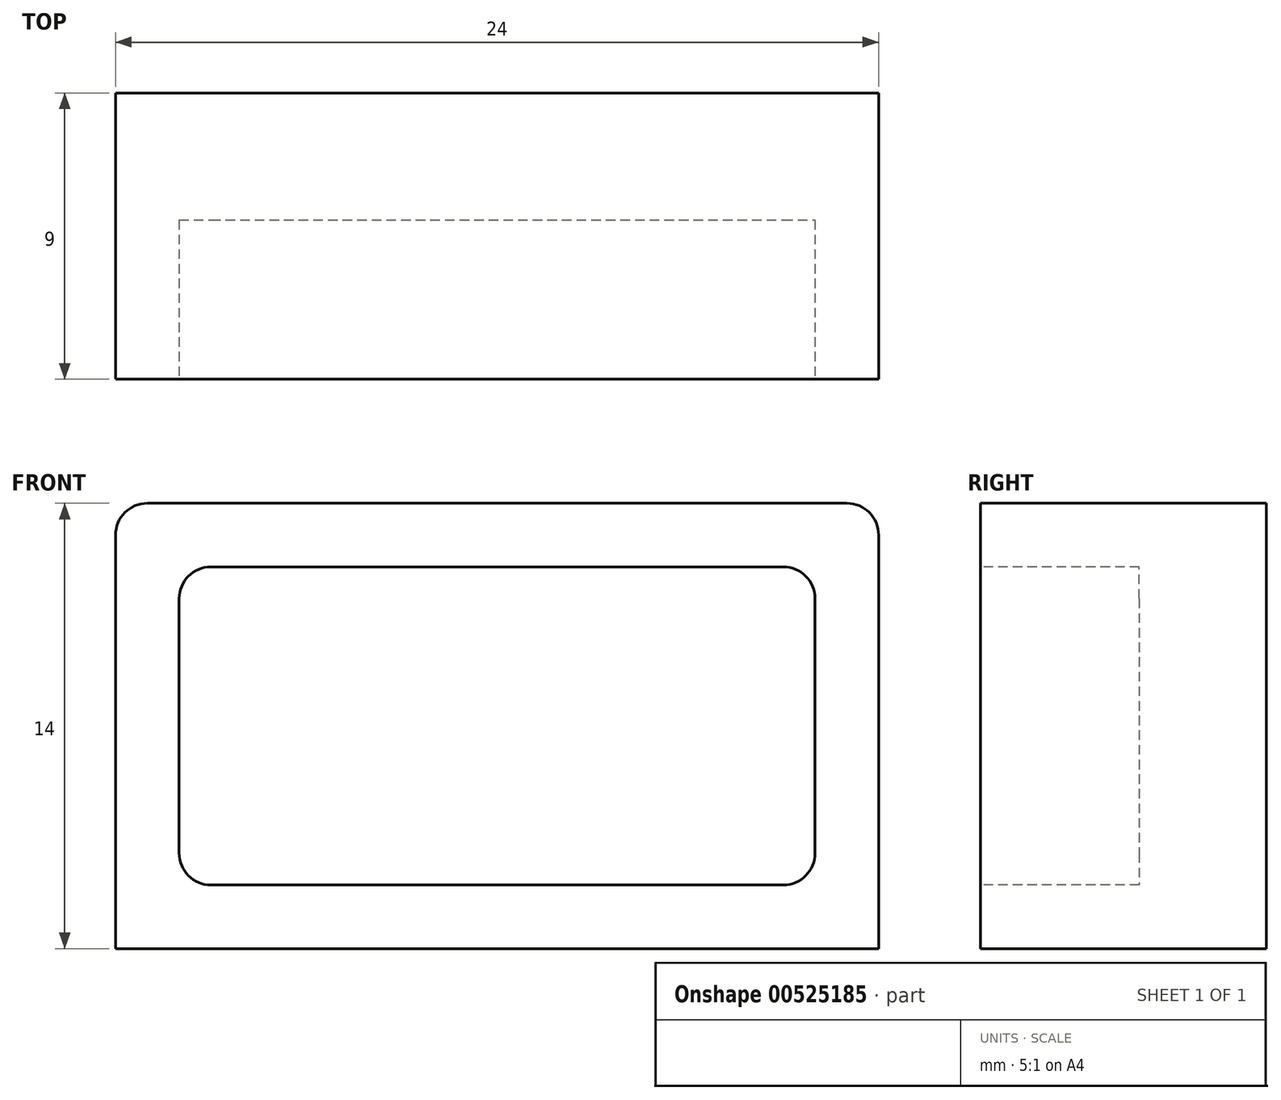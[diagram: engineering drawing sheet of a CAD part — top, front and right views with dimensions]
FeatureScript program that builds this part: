
annotation { "Feature Type Name" : "Feature", "Feature Type Description" : "" }
export const myFeature = defineFeature(function(context is Context, id is Id, definition is map)
    precondition{}
    {
        {
            assignVariable(context, id + "F0", {"name" : "DIFF", "anyValue" : 0 * mm});
        }
        {
            assignVariable(context, id + "F1", {"name" : "MAGNET_D", "anyValue" : 5 * mm + getVariable(context, 'DIFF')});
        }
        {
            assignVariable(context, id + "F2", {"name" : "PAD", "anyValue" : 2 * mm});
        }
        {
            assignVariable(context, id + "F3", {"name" : "D", "anyValue" : getVariable(context, 'MAGNET_D') + getVariable(context, 'PAD') * 2});
        }
        {
            var Q0;
            Q0=qCreatedBy(makeId("Front.planeOp"),FACE);
            var sketch = newSketch(context, id + "F4", { "sketchPlane" : qUnion([Q0])});
            skLineSegment(sketch, "E0.bottom", {"start": v(-12, 0) * mm, "end": v(12, 0) * mm});
            skLineSegment(sketch, "E0.top", {"start": v(-12, 14) * mm, "end": v(12, 14) * mm});
            skLineSegment(sketch, "E0.left", {"start": v(-12, 0) * mm, "end": v(-12, 14) * mm});
            skLineSegment(sketch, "E0.right", {"start": v(12, 0) * mm, "end": v(12, 14) * mm});
            skPoint(sketch, "E1", {"position": v(0, 0) * mm});
            skSolve(sketch);
        }
        {
            var Q0;
            Q0=makeQuery(id+"F4.imprint","IMPRINT",FACE,{"disambiguationData":[TD([[makeQuery(id+"F4.imprint","IMPRINT",EDGE,{"derivedFrom":sQuery(id+"F4.wireOp",EDGE,"E0.bottom")}),1.0]])]});
            extrude(context, id + "F5", {"entities" : qUnion([Q0]), "depth" : getVariable(context, 'D'), "offsetDistance" : 25 * mm});
        }
        {
            var Q0;
            Q0=makeQuery(id+"F5.opExtrude","CAP_FACE",FACE,{"disambiguationData":[OSD([sQuery(id+"F4.wireOp",EDGE,"E0.bottom"),sQuery(id+"F4.wireOp",EDGE,"E0.top"),sQuery(id+"F4.wireOp",EDGE,"E0.left"),sQuery(id+"F4.wireOp",EDGE,"E0.right")])],"isStart":false});
            var sketch = newSketch(context, id + "F6", { "sketchPlane" : qUnion([Q0])});
            skLineSegment(sketch, "E2.bottom", {"start": v(-10, 12) * mm, "end": v(10, 12) * mm});
            skLineSegment(sketch, "E2.top", {"start": v(-10, 2) * mm, "end": v(10, 2) * mm});
            skLineSegment(sketch, "E2.left", {"start": v(-10, 12) * mm, "end": v(-10, 2) * mm});
            skLineSegment(sketch, "E2.right", {"start": v(10, 12) * mm, "end": v(10, 2) * mm});
            skSolve(sketch);
        }
        {
            var Q0;
            Q0 = qSketchRegion(id + "F6", true);
            extrude(context, id + "F7", {"entities" : qUnion([Q0]), "operationType" : NewBodyOperationType.REMOVE, "oppositeDirection" : true, "depth" : getVariable(context, 'MAGNET_D'), "offsetDistance" : 25 * mm});
        }
        {
            var Q0;
            Q0=makeQuery(id+"F5.opExtrude","SWEPT_EDGE",EDGE,{"disambiguationData":[OSD([sQuery(id+"F4.wireOp",EDGE,"E0.top"),sQuery(id+"F4.wireOp",EDGE,"E0.left")])]});
            var Q1;
            Q1=makeQuery(id+"F5.opExtrude","SWEPT_EDGE",EDGE,{"disambiguationData":[OSD([sQuery(id+"F4.wireOp",EDGE,"E0.top"),sQuery(id+"F4.wireOp",EDGE,"E0.right")])]});
            var Q2;
            Q2=makeQuery(id+"F7.boolean.opBoolean","COPY",EDGE,{"derivedFrom":makeQuery(id+"F7.opExtrude","SWEPT_EDGE",EDGE,{"disambiguationData":[OSD([sQuery(id+"F6.wireOp",EDGE,"E2.bottom"),sQuery(id+"F6.wireOp",EDGE,"E2.left")])]})});
            var Q3;
            Q3=makeQuery(id+"F7.boolean.opBoolean","COPY",EDGE,{"derivedFrom":makeQuery(id+"F7.opExtrude","SWEPT_EDGE",EDGE,{"disambiguationData":[OSD([sQuery(id+"F6.wireOp",EDGE,"E2.bottom"),sQuery(id+"F6.wireOp",EDGE,"E2.right")])]})});
            var Q4;
            Q4=makeQuery(id+"F7.boolean.opBoolean","COPY",EDGE,{"derivedFrom":makeQuery(id+"F7.opExtrude","SWEPT_EDGE",EDGE,{"disambiguationData":[OSD([sQuery(id+"F6.wireOp",EDGE,"E2.top"),sQuery(id+"F6.wireOp",EDGE,"E2.right")])]})});
            var Q5;
            Q5=makeQuery(id+"F7.boolean.opBoolean","COPY",EDGE,{"derivedFrom":makeQuery(id+"F7.opExtrude","SWEPT_EDGE",EDGE,{"disambiguationData":[OSD([sQuery(id+"F6.wireOp",EDGE,"E2.top"),sQuery(id+"F6.wireOp",EDGE,"E2.left")])]})});
            fillet(context, id + "F8", {"entities" : qUnion([Q0, Q1, Q2, Q3, Q4, Q5]), "radius" : 1 * mm, "tangentPropagation" : true, "allowEdgeOverflow" : false});
        }
    });
